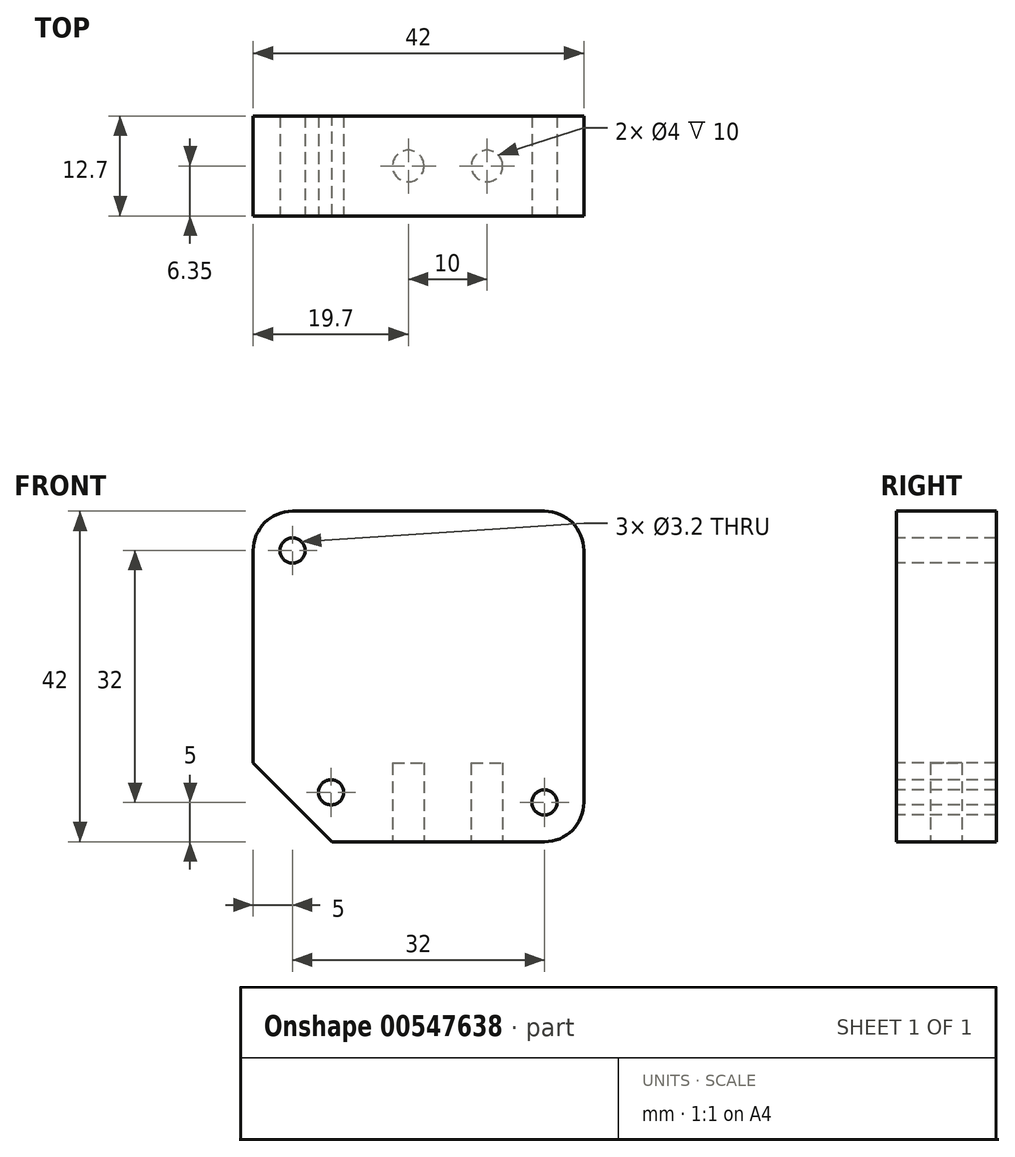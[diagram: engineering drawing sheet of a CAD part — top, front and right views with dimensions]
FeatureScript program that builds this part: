
annotation { "Feature Type Name" : "Feature", "Feature Type Description" : "" }
export const myFeature = defineFeature(function(context is Context, id is Id, definition is map)
    precondition{}
    {
        {
            var Q0;
            Q0=qCreatedBy(makeId("Front.planeOp"),FACE);
            var sketch = newSketch(context, id + "F0", { "sketchPlane" : qUnion([Q0])});
            skLineSegment(sketch, "E0.bottom", {"start": v(21, 21) * mm, "end": v(-21, 21) * mm});
            skLineSegment(sketch, "E0.top", {"start": v(21, -21) * mm, "end": v(-21, -21) * mm});
            skLineSegment(sketch, "E0.left", {"start": v(21, 21) * mm, "end": v(21, -21) * mm});
            skLineSegment(sketch, "E0.right", {"start": v(-21, 21) * mm, "end": v(-21, -21) * mm});
            skPoint(sketch, "E0.middle", {"position": v(0, 0) * mm});
            skSolve(sketch);
        }
        {
            var Q0;
            Q0 = qSketchRegion(id + "F0", true);
            extrude(context, id + "F1", {"entities" : qUnion([Q0]), "depth" : 12.7 * mm, "offsetDistance" : 25 * mm});
        }
        {
            var Q0;
            Q0=makeQuery(id+"F1.opExtrude","SWEPT_EDGE",EDGE,{"disambiguationData":[OSD([sQuery(id+"F0.wireOp",EDGE,"E0.bottom"),sQuery(id+"F0.wireOp",EDGE,"E0.left")])]});
            var Q1;
            Q1=makeQuery(id+"F1.opExtrude","SWEPT_EDGE",EDGE,{"disambiguationData":[OSD([sQuery(id+"F0.wireOp",EDGE,"E0.bottom"),sQuery(id+"F0.wireOp",EDGE,"E0.right")])]});
            var Q2;
            Q2=makeQuery(id+"F1.opExtrude","SWEPT_EDGE",EDGE,{"disambiguationData":[OSD([sQuery(id+"F0.wireOp",EDGE,"E0.top"),sQuery(id+"F0.wireOp",EDGE,"E0.left")])]});
            fillet(context, id + "F2", {"entities" : qUnion([Q0, Q1, Q2]), "radius" : 5 * mm, "tangentPropagation" : true, "allowEdgeOverflow" : false});
        }
        {
            var Q0;
            Q0=makeQuery(id+"F1.opExtrude","SWEPT_EDGE",EDGE,{"disambiguationData":[OSD([sQuery(id+"F0.wireOp",EDGE,"E0.top"),sQuery(id+"F0.wireOp",EDGE,"E0.right")])]});
            chamfer(context, id + "F3", {"entities" : qUnion([Q0]), "width" : 10 * mm, "tangentPropagation" : true});
        }
        {
            var Q0;
            Q0=makeQuery(id+"F1.opExtrude","CAP_FACE",FACE,{"disambiguationData":[OSD([sQuery(id+"F0.wireOp",EDGE,"E0.bottom"),sQuery(id+"F0.wireOp",EDGE,"E0.top"),sQuery(id+"F0.wireOp",EDGE,"E0.left"),sQuery(id+"F0.wireOp",EDGE,"E0.right")])],"isStart":false});
            var sketch = newSketch(context, id + "F4", { "sketchPlane" : qUnion([Q0])});
            skCircle(sketch, "E1", {"center": v(-16, 16) * mm, "radius": 1.6 * mm});
            skCircle(sketch, "E2", {"center": v(16, -16) * mm, "radius": 1.6 * mm});
            skCircle(sketch, "E3", {"center": v(-11.1, -14.71) * mm, "radius": 1.6 * mm});
            skSolve(sketch);
        }
        {
            var Q0;
            Q0 = qSketchRegion(id + "F4", true);
            extrude(context, id + "F5", {"entities" : qUnion([Q0]), "operationType" : NewBodyOperationType.REMOVE, "oppositeDirection" : true, "depth" : 25 * mm, "offsetDistance" : 25 * mm});
        }
        {
            var Q0;
            Q0=makeQuery(id+"F1.opExtrude","SWEPT_FACE",FACE,{"disambiguationData":[OSD([sQuery(id+"F0.wireOp",EDGE,"E0.top")])]});
            var sketch = newSketch(context, id + "F6", { "sketchPlane" : qUnion([Q0])});
            skCircle(sketch, "E4", {"center": v(8.7, 6.35) * mm, "radius": 2 * mm});
            skCircle(sketch, "E5", {"center": v(-1.3, 6.35) * mm, "radius": 2 * mm});
            skSolve(sketch);
        }
        {
            var Q0;
            Q0 = qSketchRegion(id + "F6", true);
            extrude(context, id + "F7", {"entities" : qUnion([Q0]), "operationType" : NewBodyOperationType.REMOVE, "oppositeDirection" : true, "depth" : 10 * mm, "offsetDistance" : 25 * mm});
        }
    });
